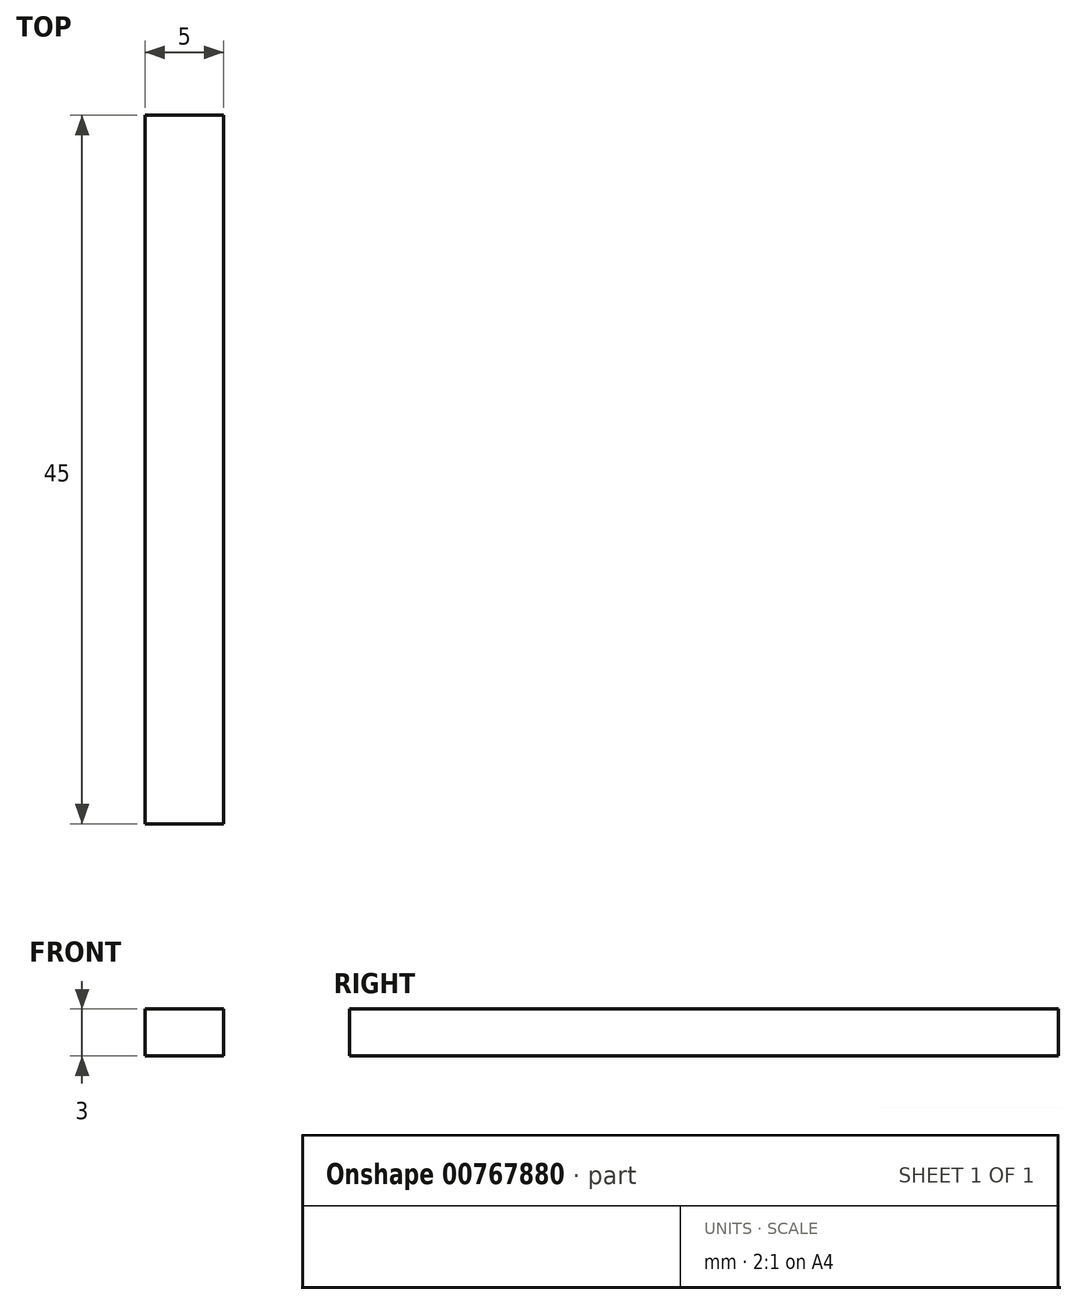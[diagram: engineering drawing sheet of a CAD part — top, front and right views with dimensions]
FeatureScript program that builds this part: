
annotation { "Feature Type Name" : "Feature", "Feature Type Description" : "" }
export const myFeature = defineFeature(function(context is Context, id is Id, definition is map)
    precondition{}
    {
        {
            var Q0;
            Q0=qCreatedBy(makeId("Front.planeOp"),FACE);
            var sketch = newSketch(context, id + "F0", { "sketchPlane" : qUnion([Q0])});
            skLineSegment(sketch, "E0.bottom", {"start": v(0, 0) * mm, "end": v(5, 0) * mm});
            skLineSegment(sketch, "E0.top", {"start": v(0, 3) * mm, "end": v(5, 3) * mm});
            skLineSegment(sketch, "E0.left", {"start": v(0, 0) * mm, "end": v(0, 3) * mm});
            skLineSegment(sketch, "E0.right", {"start": v(5, 0) * mm, "end": v(5, 3) * mm});
            skSolve(sketch);
        }
        {
            var Q0;
            Q0 = qSketchRegion(id + "F0", true);
            extrude(context, id + "F1", {"entities" : qUnion([Q0]), "depth" : 45 * mm, "offsetDistance" : 25 * mm});
        }
    });
